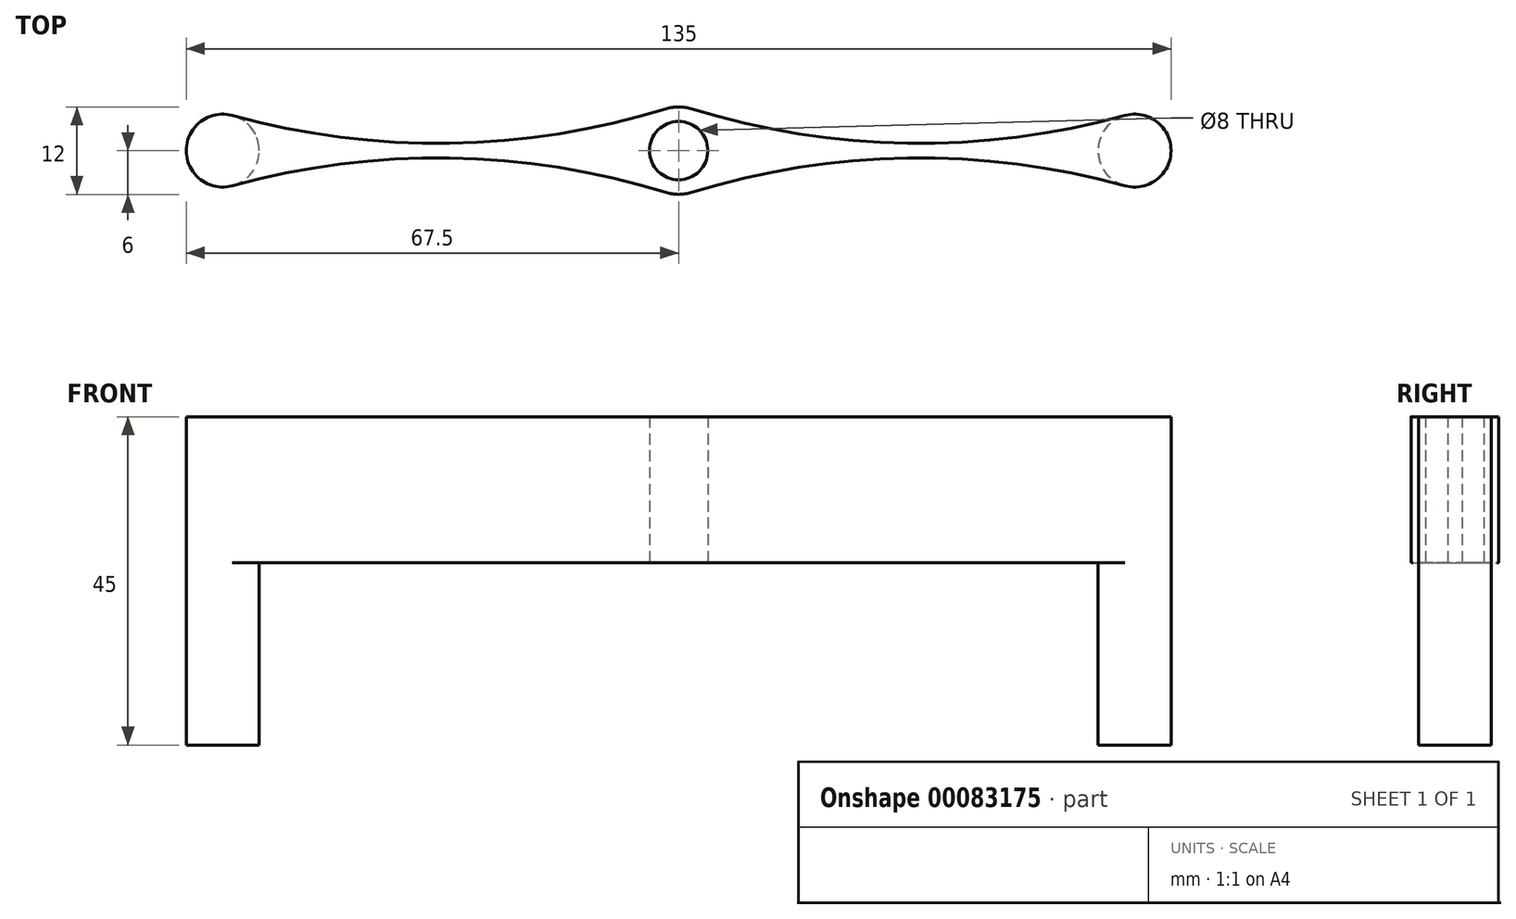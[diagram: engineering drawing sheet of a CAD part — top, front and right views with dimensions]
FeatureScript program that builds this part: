
annotation { "Feature Type Name" : "Feature", "Feature Type Description" : "" }
export const myFeature = defineFeature(function(context is Context, id is Id, definition is map)
    precondition{}
    {
        {
            var Q0;
            Q0=qCreatedBy(makeId("Top.planeOp"),FACE);
            var sketch = newSketch(context, id + "F2", { "sketchPlane" : qUnion([Q0])});
            skCircle(sketch, "E0", {"center": v(62.5, 0) * mm, "radius": 5 * mm});
            skCircle(sketch, "E1", {"center": v(-62.5, 0) * mm, "radius": 5 * mm});
            skLineSegment(sketch, "E2", {"start": v(-62.5, 0) * mm, "end": v(0, 0) * mm, "construction": true});
            skLineSegment(sketch, "E3", {"start": v(0, 0) * mm, "end": v(62.5, 0) * mm, "construction": true});
            skCircle(sketch, "E4", {"center": v(0, 0) * mm, "radius": 4 * mm});
            skCircle(sketch, "E5", {"center": v(0, 0) * mm, "radius": 6 * mm});
            skArc(sketch, "E6", {"start": v(-61.17, 4.82) * mm, "mid": v(-31.4, 1.01) * mm, "end": v(-1.78, 5.73) * mm});
            skArc(sketch, "E7", {"start": v(-1.78, -5.73) * mm, "mid": v(-31.4, -1.01) * mm, "end": v(-61.17, -4.82) * mm});
            skArc(sketch, "E8", {"start": v(1.78, 5.73) * mm, "mid": v(31.4, 1.01) * mm, "end": v(61.17, 4.82) * mm});
            skArc(sketch, "E9", {"start": v(61.17, -4.82) * mm, "mid": v(31.4, -1.01) * mm, "end": v(1.78, -5.73) * mm});
            skSolve(sketch);
        }
        {
            var Q0;
            Q0=makeQuery(id+"F2.imprint","IMPRINT",FACE,{"disambiguationData":[TD([[makeQuery(id+"F2.imprint","IMPRINT",EDGE,{"derivedFrom":sQuery(id+"F2.wireOp",EDGE,"E4")}),-1.0]])]});
            var Q1;
            {var subQ0=sQuery(id+"F2.wireOp",EDGE,"E8");Q1=makeQuery(id+"F2.imprint","IMPRINT",FACE,{"disambiguationData":[TD([[makeQuery(id+"F2.imprint","IMPRINT",EDGE,{"derivedFrom":subQ0}),-1.0]])]});}
            var Q2;
            {var subQ0=sQuery(id+"F2.wireOp",EDGE,"E6");Q2=makeQuery(id+"F2.imprint","IMPRINT",FACE,{"disambiguationData":[TD([[makeQuery(id+"F2.imprint","IMPRINT",EDGE,{"derivedFrom":subQ0}),-1.0]])]});}
            var Q3;
            {var subQ0=sQuery(id+"F2.wireOp",EDGE,"E1");var subQ1=makeQuery(id+"F2.imprint","INTERSECT",VERTEX,{"derivedFrom":[subQ0,sQuery(id+"F2.wireOp",EDGE,"E6")]});Q3=makeQuery(id+"F2.imprint","IMPRINT",FACE,{"disambiguationData":[TD([[makeQuery(id+"F2.imprint","IMPRINT",EDGE,{"disambiguationData":[TD([[subQ1,-1.0]])],"derivedFrom":subQ0}),1.0]])]});}
            var Q4;
            {var subQ0=sQuery(id+"F2.wireOp",EDGE,"E0");var subQ1=makeQuery(id+"F2.imprint","INTERSECT",VERTEX,{"derivedFrom":[subQ0,sQuery(id+"F2.wireOp",EDGE,"E8")]});Q4=makeQuery(id+"F2.imprint","IMPRINT",FACE,{"disambiguationData":[TD([[makeQuery(id+"F2.imprint","IMPRINT",EDGE,{"disambiguationData":[TD([[subQ1,-1.0]])],"derivedFrom":subQ0}),1.0]])]});}
            extrude(context, id + "F0", {"entities" : qUnion([Q0, Q1, Q2, Q3, Q4]), "depth" : 20 * mm});
        }
        {
            var Q0;
            {var subQ0=sQuery(id+"F2.wireOp",EDGE,"E0");var subQ1=makeQuery(id+"F2.imprint","INTERSECT",VERTEX,{"derivedFrom":[subQ0,sQuery(id+"F2.wireOp",EDGE,"be418fcc-0dd0-4e3b-a223-f21b005c060b")]});Q0=makeQuery(id+"F2.imprint","IMPRINT",FACE,{"disambiguationData":[TD([[makeQuery(id+"F2.imprint","IMPRINT",EDGE,{"disambiguationData":[TD([[subQ1,-1.0]])],"derivedFrom":subQ0}),1.0]])]});}
            var Q1;
            {var subQ0=sQuery(id+"F2.wireOp",EDGE,"E1");var subQ1=makeQuery(id+"F2.imprint","INTERSECT",VERTEX,{"derivedFrom":[subQ0,sQuery(id+"F2.wireOp",EDGE,"be418fcc-0dd0-4e3b-a223-f21b005c060b")]});Q1=makeQuery(id+"F2.imprint","IMPRINT",FACE,{"disambiguationData":[TD([[makeQuery(id+"F2.imprint","IMPRINT",EDGE,{"disambiguationData":[TD([[subQ1,-1.0]])],"derivedFrom":subQ0}),1.0]])]});}
            extrude(context, id + "F1", {"entities" : qUnion([Q0, Q1]), "operationType" : NewBodyOperationType.ADD, "oppositeDirection" : true, "depth" : 25 * mm});
        }
    });
